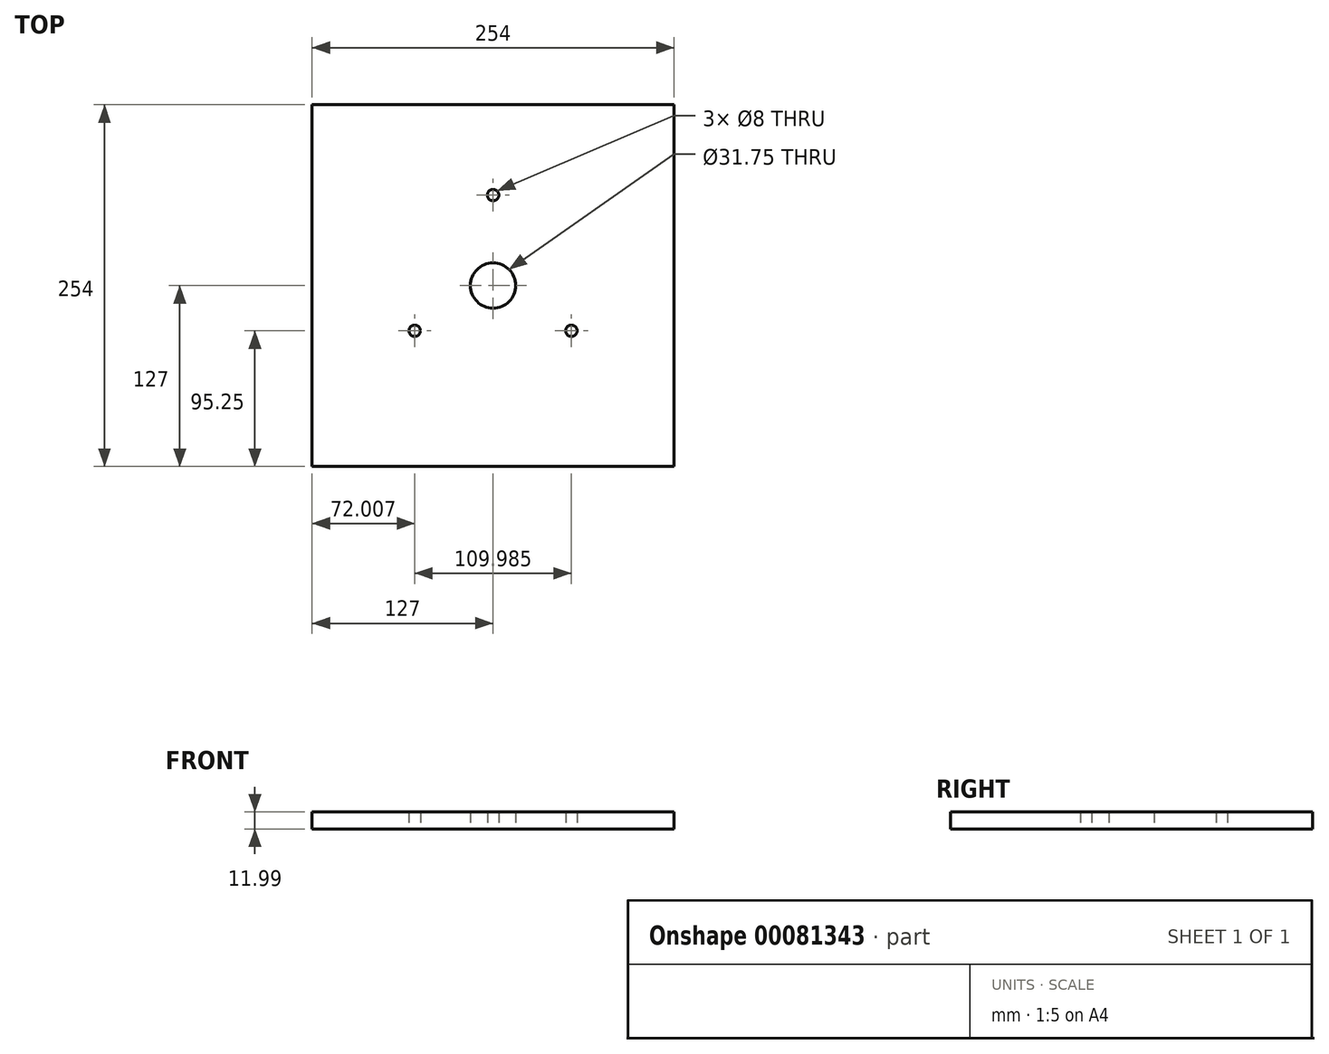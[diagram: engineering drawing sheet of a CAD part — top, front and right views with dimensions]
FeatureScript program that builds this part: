
annotation { "Feature Type Name" : "Feature", "Feature Type Description" : "" }
export const myFeature = defineFeature(function(context is Context, id is Id, definition is map)
    precondition{}
    {
        {
            var Q0;
            Q0=qCreatedBy(makeId("Top.planeOp"),FACE);
            var sketch = newSketch(context, id + "F0", { "sketchPlane" : qUnion([Q0])});
            skLineSegment(sketch, "E0", {"start": v(-127, 127) * mm, "end": v(-127, -127) * mm});
            skLineSegment(sketch, "E1", {"start": v(-127, -127) * mm, "end": v(127, -127) * mm});
            skLineSegment(sketch, "E2", {"start": v(127, -127) * mm, "end": v(127, 127) * mm});
            skLineSegment(sketch, "E3", {"start": v(127, 127) * mm, "end": v(-127, 127) * mm});
            skCircle(sketch, "E4", {"center": v(0, 0) * mm, "radius": 15.88 * mm});
            skCircle(sketch, "E5", {"center": v(0, 63.5) * mm, "radius": 4 * mm});
            skPoint(sketch, "E6", {"position": v(0, 127) * mm});
            skPoint(sketch, "E7", {"position": v(127, 0) * mm});
            skPoint(sketch, "E8", {"position": v(0, -127) * mm});
            skPoint(sketch, "E9", {"position": v(-127, 0) * mm});
            skCircle(sketch, "E10.1.0", {"center": v(-55, -31.75) * mm, "radius": 4 * mm});
            skCircle(sketch, "E10.2.0", {"center": v(55, -31.75) * mm, "radius": 4 * mm});
            skSolve(sketch);
        }
        {
            var Q0;
            Q0=makeQuery(id+"F0.imprint","IMPRINT",FACE,{"disambiguationData":[TD([[makeQuery(id+"F0.imprint","IMPRINT",EDGE,{"derivedFrom":sQuery(id+"F0.wireOp",EDGE,"E0")}),1.0]])]});
            extrude(context, id + "F1", {"entities" : qUnion([Q0]), "depth" : 12 * mm, "offsetDistance" : 25.4 * mm});
        }
    });
